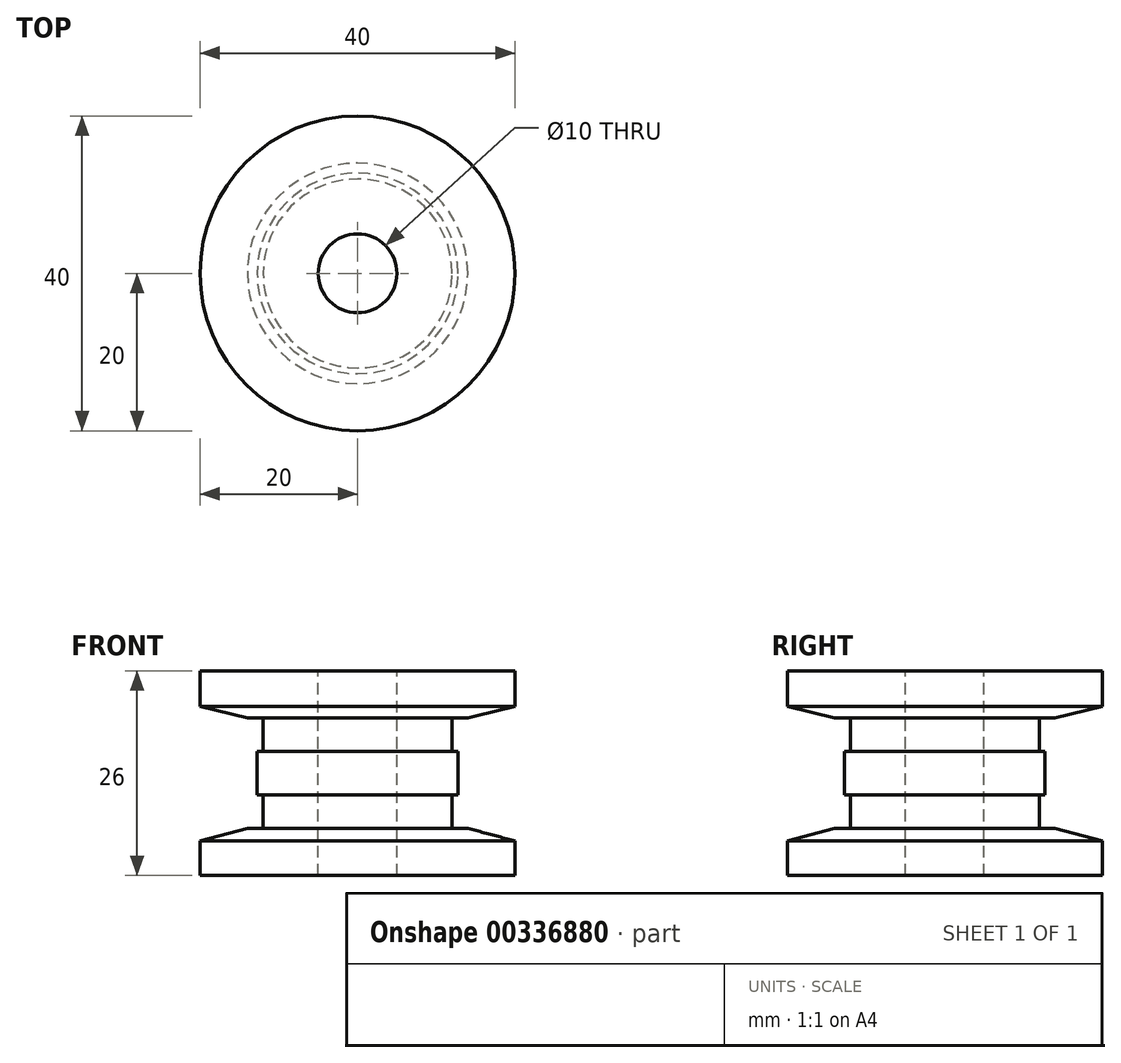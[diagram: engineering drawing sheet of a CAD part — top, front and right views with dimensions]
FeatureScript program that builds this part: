
annotation { "Feature Type Name" : "Feature", "Feature Type Description" : "" }
export const myFeature = defineFeature(function(context is Context, id is Id, definition is map)
    precondition{}
    {
        {
            var Q0;
            Q0=qCreatedBy(makeId("Top.planeOp"),FACE);
            var sketch = newSketch(context, id + "F0", { "sketchPlane" : qUnion([Q0])});
            skCircle(sketch, "E0", {"center": v(0, 0) * mm, "radius": 20 * mm});
            skSolve(sketch);
        }
        {
            var Q0;
            Q0 = qSketchRegion(id + "F0", true);
            extrude(context, id + "F1", {"entities" : qUnion([Q0]), "depth" : 6 * mm});
        }
        {
            var Q0;
            Q0=makeQuery(id+"F1.opExtrude","CAP_FACE",FACE,{"disambiguationData":[OSD([sQuery(id+"F0.wireOp",EDGE,"E0")])],"isStart":false});
            var sketch = newSketch(context, id + "F2", { "sketchPlane" : qUnion([Q0])});
            skCircle(sketch, "E1", {"center": v(0, 0) * mm, "radius": 12 * mm});
            skSolve(sketch);
        }
        {
            var Q0;
            Q0 = qSketchRegion(id + "F2", true);
            extrude(context, id + "F3", {"entities" : qUnion([Q0]), "operationType" : NewBodyOperationType.ADD, "depth" : 4.25 * mm});
        }
        {
            var Q0;
            Q0=makeQuery(id+"F3.opExtrude","CAP_FACE",FACE,{"disambiguationData":[OSD([sQuery(id+"F2.wireOp",EDGE,"E1")])],"isStart":false});
            var sketch = newSketch(context, id + "F4", { "sketchPlane" : qUnion([Q0])});
            skCircle(sketch, "E2", {"center": v(0, 0) * mm, "radius": 12.75 * mm});
            skSolve(sketch);
        }
        {
            var Q0;
            Q0 = qSketchRegion(id + "F4", true);
            extrude(context, id + "F5", {"entities" : qUnion([Q0]), "operationType" : NewBodyOperationType.ADD, "depth" : 5.5 * mm});
        }
        {
            var Q0;
            Q0=makeQuery(id+"F5.opExtrude","CAP_FACE",FACE,{"disambiguationData":[OSD([sQuery(id+"F4.wireOp",EDGE,"E2")])],"isStart":false});
            var sketch = newSketch(context, id + "F6", { "sketchPlane" : qUnion([Q0])});
            skCircle(sketch, "E3", {"center": v(0, 0) * mm, "radius": 12 * mm});
            skSolve(sketch);
        }
        {
            var Q0;
            Q0 = qSketchRegion(id + "F6", true);
            extrude(context, id + "F7", {"entities" : qUnion([Q0]), "operationType" : NewBodyOperationType.ADD, "depth" : 4.25 * mm});
        }
        {
            var Q0;
            Q0=makeQuery(id+"F7.opExtrude","CAP_FACE",FACE,{"disambiguationData":[OSD([sQuery(id+"F6.wireOp",EDGE,"E3")])],"isStart":false});
            var sketch = newSketch(context, id + "F8", { "sketchPlane" : qUnion([Q0])});
            skCircle(sketch, "E4", {"center": v(0, 0) * mm, "radius": 20 * mm});
            skSolve(sketch);
        }
        {
            var Q0;
            Q0 = qSketchRegion(id + "F8", true);
            extrude(context, id + "F9", {"entities" : qUnion([Q0]), "operationType" : NewBodyOperationType.ADD, "depth" : 6 * mm});
        }
        {
            var Q0;
            Q0=makeQuery(id+"F9.opExtrude","CAP_FACE",FACE,{"disambiguationData":[OSD([sQuery(id+"F8.wireOp",EDGE,"E4")])],"isStart":false});
            var sketch = newSketch(context, id + "F10", { "sketchPlane" : qUnion([Q0])});
            skCircle(sketch, "E5", {"center": v(0, 0) * mm, "radius": 5 * mm});
            skSolve(sketch);
        }
        {
            var Q0;
            Q0 = qSketchRegion(id + "F10", true);
            extrude(context, id + "F11", {"entities" : qUnion([Q0]), "operationType" : NewBodyOperationType.REMOVE, "endBound" : BoundingType.THROUGH_ALL, "oppositeDirection" : true, "depth" : 25 * mm});
        }
        {
            var Q0;
            Q0=makeQuery(id+"F1.opExtrude","CAP_EDGE",EDGE,{"disambiguationData":[OSD([sQuery(id+"F0.wireOp",EDGE,"E0")])],"isStart":false});
            chamfer(context, id + "F12", {"entities" : qUnion([Q0]), "chamferType" : ChamferType.TWO_OFFSETS, "width1" : 6 * mm, "oppositeDirection" : false, "width2" : 1.6 * mm, "tangentPropagation" : true});
        }
        {
            var Q0;
            Q0=makeQuery(id+"F9.opExtrude","CAP_EDGE",EDGE,{"disambiguationData":[OSD([sQuery(id+"F8.wireOp",EDGE,"E4")])],"isStart":true});
            chamfer(context, id + "F13", {"entities" : qUnion([Q0]), "chamferType" : ChamferType.TWO_OFFSETS, "width1" : 1.5 * mm, "oppositeDirection" : false, "width2" : 6 * mm, "tangentPropagation" : true});
        }
    });
